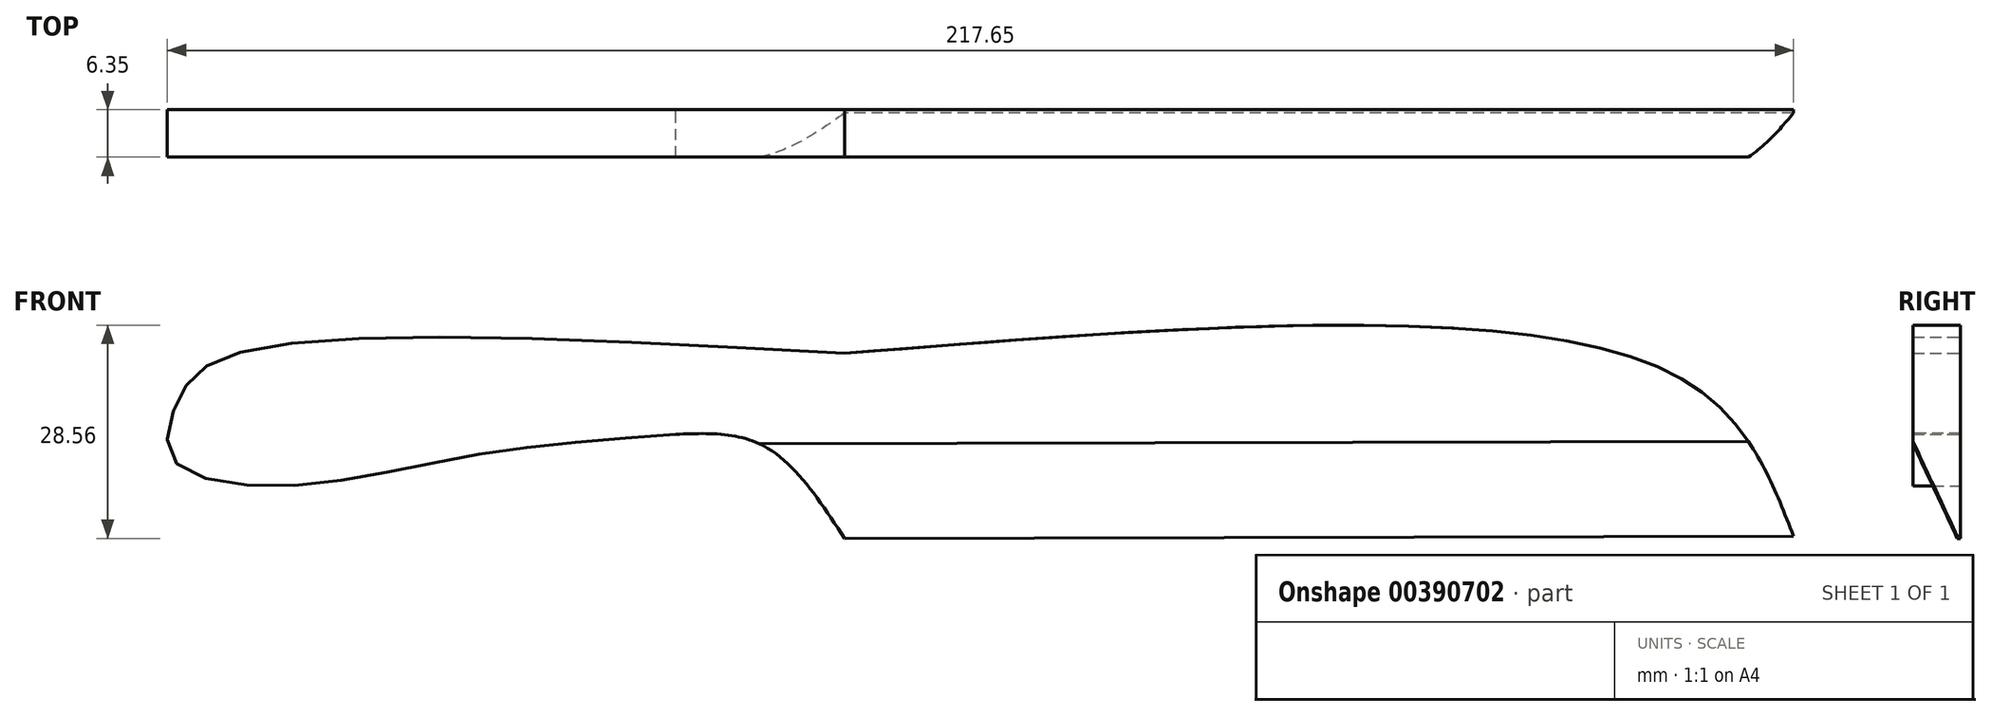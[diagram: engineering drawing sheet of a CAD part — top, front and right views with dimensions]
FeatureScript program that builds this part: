
annotation { "Feature Type Name" : "Feature", "Feature Type Description" : "" }
export const myFeature = defineFeature(function(context is Context, id is Id, definition is map)
    precondition{}
    {
        {
            var Q0;
            Q0=qCreatedBy(makeId("Front.planeOp"),FACE);
            var sketch = newSketch(context, id + "F0", { "sketchPlane" : qUnion([Q0])});
            skFitSpline(sketch, "E0", {"points": [v(66.97, 10.55) * mm, v(50.86, 32.24) * mm, v(-60.03, 35.02) * mm], "startDerivative": vector(-29.44, 75.78) * mm, "endDerivative": vector(-204.74, -16.41) * mm});
            skLineSegment(sketch, "E1", {"start": v(-60.03, 35.02) * mm, "end": v(-60.03, 10.24) * mm});
            skLineSegment(sketch, "E2", {"start": v(-60.03, 10.24) * mm, "end": v(66.97, 10.55) * mm});
            skFitSpline(sketch, "E3", {"points": [v(-60.03, 35.02) * mm, v(-141.5, 35.02) * mm, v(-149.24, 28.83) * mm, v(-149.86, 20.78) * mm, v(-133.44, 17.37) * mm, v(-109.6, 21.4) * mm, v(-82.64, 24.18) * mm], "startDerivative": vector(-333.48, 18.32) * mm, "endDerivative": vector(154.89, 11.03) * mm});
            skPoint(sketch, "E4.1.internal.snap0", {"position": v(-60.03, 22.63) * mm});
            skFitSpline(sketch, "E4", {"points": [v(-82.64, 24.18) * mm, v(-70.87, 22.63) * mm, v(-60.03, 10.24) * mm], "startDerivative": vector(26.91, 1.11) * mm, "endDerivative": vector(18.54, -28.2) * mm});
            skSolve(sketch);
        }
        {
            var Q0;
            Q0 = qSketchRegion(id + "F0", true);
            extrude(context, id + "F1", {"entities" : qUnion([Q0]), "depth" : 6.35 * mm});
        }
        {
            var Q0;
            Q0=makeQuery(id+"F1.opExtrude","CAP_EDGE",EDGE,{"disambiguationData":[OSD([sQuery(id+"F0.wireOp",EDGE,"E2")])],"isStart":false});
            chamfer(context, id + "F2", {"entities" : qUnion([Q0]), "chamferType" : ChamferType.OFFSET_ANGLE, "width" : 12.7 * mm, "oppositeDirection" : false, "angle" : 25 * degree, "tangentPropagation" : true});
        }
    });
